# Revit family: LINEAL 6W II ASIMETRICA_EM6AW.1
name_source: partatom
category: Luminarias
units: mm (PartAtom-declared; Revit-internal decimal feet)

## family parameters
Compartido = No
Corte con vacíos al cargar = No
Cota de conector redondo = Diámetro de uso
Origen de luz = Sí
Punto de cálculo de habitación = No
Se basa en plano de trabajo = Sí
Siempre vertical = No
Tipo de pieza = Normal

## types (1)
- EMP_EM6AW.1
    Cambio de temperatura de color de luz atenuada = Curva de lámpara incandescente
    Comentarios de vataje = 100-240V
    Descripción = LUMINARIA PARA EMPOTRAR TIPO LINEAL CON 3 LED TIPO OSRAM CON UNA POTENCIA DE 6W, CUERPO DE ALUMINIO FUNDIDO A PRESION CUBIERTO CON POLVO GRIS OSCURO CON CUBIERTA DE ACERO INOXIDABLE Y VIDRIO TEMPLADO DE 8MM, PLACAS DE PVC PARA INSTALACION POR COLADO Y EVITAR DEFORMACIONES EN EL HOUSING (MATERIAL ABS), CON UNA DIMENSION DE 90MM DE PROFUNDO POR 195 DE LARGO EN LA LUMINARIA, CUENTA CON 333 LUMENES A UNA TEMPERATURA EN BLANCO CALIDO DE 3000K, CORRIENTE DE OPERACIÓN A 89mA, ON/OFF, DIMEABLE EN TRIAC (OPCIONAL), CABLE H05RN L0.5M, IRC 80, IK08, IP67, ANGULO DE APERTURA ASIMETRICA 45X35 GRADOS EN STOCK ALIMENTADA A 100-240V.
    Elevación por defecto = 0 mm  [stored 0 ft]
    Fabricante = BRILLANT
    Filtro de color = 16777215
    Longitud de línea de emisión = 100 mm  [stored 0.328084 ft]
    Longitud de símbolo de origen de luz = 3048 mm  [stored 10 ft]
    Lámpara = Osram
    Modelo = EM6AW.1
    Watt per fixture = 6
    Ángulo de campo de foco = 90.00°
    Ángulo de enfoque = 45.00°
    Ángulo de inclinación = 35.00°

note: [stored X ft] marks values corroborated as IEEE doubles in the binary element streams (Revit-internal decimal feet)

## geometry (parser evidence)
native form markers: Blend x2
no freeform markers — native parametric forms only
